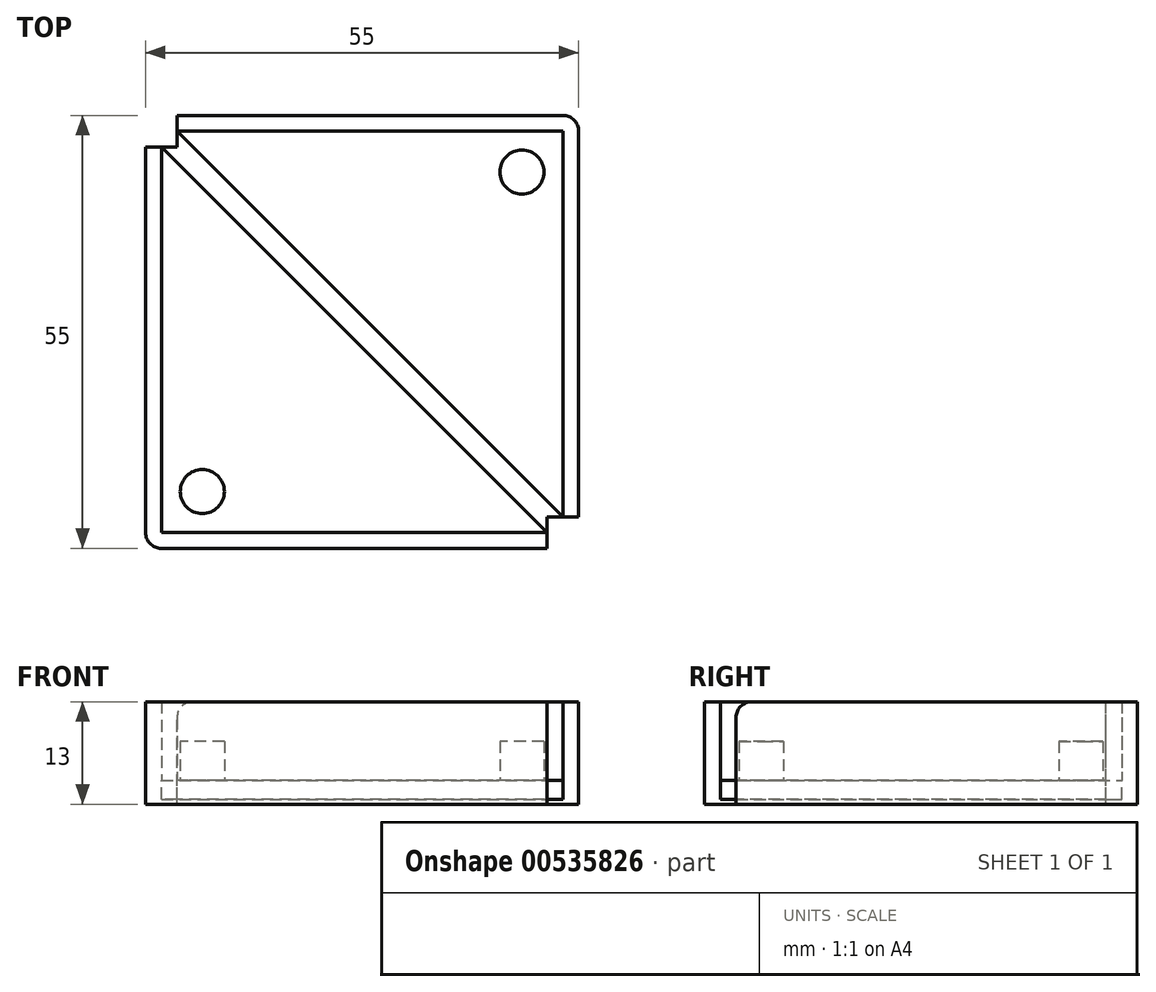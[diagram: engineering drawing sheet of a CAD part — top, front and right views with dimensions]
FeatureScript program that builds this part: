
annotation { "Feature Type Name" : "Feature", "Feature Type Description" : "" }
export const myFeature = defineFeature(function(context is Context, id is Id, definition is map)
    precondition{}
    {
        {
            var Q0;
            Q0=qCreatedBy(makeId("Top.planeOp"),FACE);
            var sketch = newSketch(context, id + "F0", { "sketchPlane" : qUnion([Q0])});
            skLineSegment(sketch, "E0.bottom", {"start": v(27.5, -27.5) * mm, "end": v(-27.5, -27.5) * mm});
            skLineSegment(sketch, "E0.top", {"start": v(27.5, 27.5) * mm, "end": v(-27.5, 27.5) * mm});
            skLineSegment(sketch, "E0.left", {"start": v(27.5, -27.5) * mm, "end": v(27.5, 27.5) * mm});
            skLineSegment(sketch, "E0.right", {"start": v(-27.5, -27.5) * mm, "end": v(-27.5, 27.5) * mm});
            skPoint(sketch, "E0.middle", {"position": v(0, 0) * mm});
            skSolve(sketch);
        }
        {
            var Q0;
            Q0=qSketchRegion(id+"F0",true);
            extrude(context, id + "F1", {"entities" : qUnion([Q0]), "depth" : 3 * mm, "offsetDistance" : 25 * mm});
        }
        {
            var Q0;
            Q0=makeQuery(id+"F1.opExtrude","CAP_FACE",FACE,{"disambiguationData":[OSD([sQuery(id+"F0.wireOp",EDGE,"E0.bottom"),sQuery(id+"F0.wireOp",EDGE,"E0.top"),sQuery(id+"F0.wireOp",EDGE,"E0.left"),sQuery(id+"F0.wireOp",EDGE,"E0.right")])],"isStart":false});
            var sketch = newSketch(context, id + "F2", { "sketchPlane" : qUnion([Q0])});
            skLineSegment(sketch, "E1.bottom", {"start": v(27.5, -27.5) * mm, "end": v(-27.5, -27.5) * mm});
            skLineSegment(sketch, "E1.top", {"start": v(27.5, 27.5) * mm, "end": v(-27.5, 27.5) * mm});
            skLineSegment(sketch, "E1.left", {"start": v(27.5, -27.5) * mm, "end": v(27.5, 27.5) * mm});
            skLineSegment(sketch, "E1.right", {"start": v(-27.5, -27.5) * mm, "end": v(-27.5, 27.5) * mm});
            skPoint(sketch, "E1.middle", {"position": v(0, 0) * mm});
            skLineSegment(sketch, "E2.bottom", {"start": v(25.5, -25.5) * mm, "end": v(-25.5, -25.5) * mm});
            skLineSegment(sketch, "E2.top", {"start": v(25.5, 25.5) * mm, "end": v(-25.5, 25.5) * mm});
            skLineSegment(sketch, "E2.left", {"start": v(25.5, -25.5) * mm, "end": v(25.5, 25.5) * mm});
            skLineSegment(sketch, "E2.right", {"start": v(-25.5, -25.5) * mm, "end": v(-25.5, 25.5) * mm});
            skSolve(sketch);
        }
        {
            var Q0;
            Q0=qSketchRegion(id+"F2",true);
            extrude(context, id + "F3", {"entities" : qUnion([Q0]), "operationType" : NewBodyOperationType.ADD, "depth" : 10 * mm, "offsetDistance" : 25 * mm});
        }
        {
            var Q0;
            Q0=makeQuery(id+"F1.opExtrude","CAP_FACE",FACE,{"disambiguationData":[OSD([sQuery(id+"F0.wireOp",EDGE,"E0.bottom"),sQuery(id+"F0.wireOp",EDGE,"E0.top"),sQuery(id+"F0.wireOp",EDGE,"E0.left"),sQuery(id+"F0.wireOp",EDGE,"E0.right")])],"isStart":false});
            var sketch = newSketch(context, id + "F4", { "sketchPlane" : qUnion([Q0])});
            skCircle(sketch, "E3", {"center": v(-20.3, -20.3) * mm, "radius": 2.8 * mm});
            skCircle(sketch, "E4", {"center": v(20.3, 20.3) * mm, "radius": 2.8 * mm});
            skSolve(sketch);
        }
        {
            var Q0;
            Q0=qSketchRegion(id+"F4",true);
            extrude(context, id + "F5", {"entities" : qUnion([Q0]), "operationType" : NewBodyOperationType.ADD, "depth" : 5 * mm, "offsetDistance" : 25 * mm});
        }
        {
            var Q0;
            Q0=makeQuery(id+"F3.opExtrude","CAP_FACE",FACE,{"disambiguationData":[OSD([sQuery(id+"F2.wireOp",EDGE,"E1.bottom"),sQuery(id+"F2.wireOp",EDGE,"E1.top"),sQuery(id+"F2.wireOp",EDGE,"E1.left"),sQuery(id+"F2.wireOp",EDGE,"E1.right"),sQuery(id+"F2.wireOp",EDGE,"E2.bottom"),sQuery(id+"F2.wireOp",EDGE,"E2.top"),sQuery(id+"F2.wireOp",EDGE,"E2.left"),sQuery(id+"F2.wireOp",EDGE,"E2.right")])],"isStart":false});
            var sketch = newSketch(context, id + "F6", { "sketchPlane" : qUnion([Q0])});
            skLineSegment(sketch, "E5.bottom", {"start": v(-27.5, 27.5) * mm, "end": v(-23.5, 27.5) * mm});
            skLineSegment(sketch, "E5.top", {"start": v(-27.5, 23.5) * mm, "end": v(-23.5, 23.5) * mm});
            skLineSegment(sketch, "E5.left", {"start": v(-27.5, 27.5) * mm, "end": v(-27.5, 23.5) * mm});
            skLineSegment(sketch, "E5.right", {"start": v(-23.5, 27.5) * mm, "end": v(-23.5, 23.5) * mm});
            skLineSegment(sketch, "E6.bottom", {"start": v(27.5, -27.5) * mm, "end": v(23.5, -27.5) * mm});
            skLineSegment(sketch, "E6.top", {"start": v(27.5, -23.5) * mm, "end": v(23.5, -23.5) * mm});
            skLineSegment(sketch, "E6.left", {"start": v(27.5, -27.5) * mm, "end": v(27.5, -23.5) * mm});
            skLineSegment(sketch, "E6.right", {"start": v(23.5, -27.5) * mm, "end": v(23.5, -23.5) * mm});
            skSolve(sketch);
        }
        {
            var Q0;
            Q0=qSketchRegion(id+"F6",true);
            extrude(context, id + "F7", {"entities" : qUnion([Q0]), "operationType" : NewBodyOperationType.REMOVE, "oppositeDirection" : true, "depth" : 25 * mm, "offsetDistance" : 25 * mm});
        }
        {
            var Q0;
            Q0=makeQuery(id+"F1.opExtrude","CAP_FACE",FACE,{"disambiguationData":[OSD([sQuery(id+"F0.wireOp",EDGE,"E0.bottom"),sQuery(id+"F0.wireOp",EDGE,"E0.top"),sQuery(id+"F0.wireOp",EDGE,"E0.left"),sQuery(id+"F0.wireOp",EDGE,"E0.right")])],"isStart":false});
            var sketch = newSketch(context, id + "F8", { "sketchPlane" : qUnion([Q0])});
            skLineSegment(sketch, "E7", {"start": v(-25.5, 23.5) * mm, "end": v(23.5, -25.5) * mm});
            skLineSegment(sketch, "E8", {"start": v(23.5, -25.5) * mm, "end": v(25.5, -23.5) * mm});
            skLineSegment(sketch, "E9", {"start": v(25.5, -23.5) * mm, "end": v(-23.5, 25.5) * mm});
            skLineSegment(sketch, "E10", {"start": v(-23.5, 25.5) * mm, "end": v(-25.5, 23.5) * mm});
            skSolve(sketch);
        }
        {
            var Q0;
            Q0=qSketchRegion(id+"F8",true);
            extrude(context, id + "F9", {"entities" : qUnion([Q0]), "operationType" : NewBodyOperationType.REMOVE, "oppositeDirection" : true, "depth" : 2.4 * mm, "offsetDistance" : 25 * mm});
        }
        {
            var Q0;
            Q0=makeQuery(id+"F7.boolean.opBoolean","COPY",EDGE,{"derivedFrom":makeQuery(id+"F7.opExtrude","CAP_EDGE",EDGE,{"disambiguationData":[OSD([sQuery(id+"F6.wireOp",EDGE,"E5.top")])],"isStart":true})});
            var Q1;
            Q1=makeQuery(id+"F7.boolean.opBoolean","COPY",EDGE,{"derivedFrom":makeQuery(id+"F7.opExtrude","CAP_EDGE",EDGE,{"disambiguationData":[OSD([sQuery(id+"F6.wireOp",EDGE,"E6.right")])],"isStart":true})});
            var Q2;
            Q2=makeQuery(id+"F7.boolean.opBoolean","COPY",EDGE,{"derivedFrom":makeQuery(id+"F7.opExtrude","CAP_EDGE",EDGE,{"disambiguationData":[OSD([sQuery(id+"F6.wireOp",EDGE,"E6.top")])],"isStart":true})});
            var Q3;
            Q3=makeQuery(id+"F7.boolean.opBoolean","COPY",EDGE,{"derivedFrom":makeQuery(id+"F7.opExtrude","CAP_EDGE",EDGE,{"disambiguationData":[OSD([sQuery(id+"F6.wireOp",EDGE,"E5.right")])],"isStart":true})});
            var Q4;
            Q4=makeQuery(id+"F7.boolean.opBoolean","COPY",EDGE,{"derivedFrom":makeQuery(id+"F7.opExtrude","SWEPT_EDGE",EDGE,{"disambiguationData":[OSD([sQuery(id+"F2.wireOp",EDGE,"E1.right"),sQuery(id+"F6.wireOp",EDGE,"E5.top"),sQuery(id+"F6.wireOp",EDGE,"E5.left")])]})});
            var Q5;
            Q5=makeQuery(id+"F7.boolean.opBoolean","COPY",EDGE,{"derivedFrom":makeQuery(id+"F7.opExtrude","SWEPT_EDGE",EDGE,{"disambiguationData":[OSD([sQuery(id+"F2.wireOp",EDGE,"E1.top"),sQuery(id+"F6.wireOp",EDGE,"E5.bottom"),sQuery(id+"F6.wireOp",EDGE,"E5.right")])]})});
            var Q6;
            Q6=makeQuery(id+"F7.boolean.opBoolean","COPY",EDGE,{"derivedFrom":makeQuery(id+"F7.opExtrude","SWEPT_EDGE",EDGE,{"disambiguationData":[OSD([sQuery(id+"F2.wireOp",EDGE,"E1.bottom"),sQuery(id+"F6.wireOp",EDGE,"E6.bottom"),sQuery(id+"F6.wireOp",EDGE,"E6.right")])]})});
            var Q7;
            Q7=makeQuery(id+"F7.boolean.opBoolean","COPY",EDGE,{"derivedFrom":makeQuery(id+"F7.opExtrude","SWEPT_EDGE",EDGE,{"disambiguationData":[OSD([sQuery(id+"F2.wireOp",EDGE,"E1.left"),sQuery(id+"F6.wireOp",EDGE,"E6.top"),sQuery(id+"F6.wireOp",EDGE,"E6.left")])]})});
            var Q8;
            Q8=makeQuery(id+"F3.boolean.opBoolean","MERGE",EDGE,{"derivedFrom":[makeQuery(id+"F1.opExtrude","SWEPT_EDGE",EDGE,{"disambiguationData":[OSD([sQuery(id+"F0.wireOp",EDGE,"E0.bottom"),sQuery(id+"F0.wireOp",EDGE,"E0.right")])]}),makeQuery(id+"F3.opExtrude","SWEPT_EDGE",EDGE,{"disambiguationData":[OSD([sQuery(id+"F2.wireOp",EDGE,"E1.bottom"),sQuery(id+"F2.wireOp",EDGE,"E1.right")])]})]});
            var Q9;
            Q9=makeQuery(id+"F3.boolean.opBoolean","MERGE",EDGE,{"derivedFrom":[makeQuery(id+"F1.opExtrude","SWEPT_EDGE",EDGE,{"disambiguationData":[OSD([sQuery(id+"F0.wireOp",EDGE,"E0.top"),sQuery(id+"F0.wireOp",EDGE,"E0.left")])]}),makeQuery(id+"F3.opExtrude","SWEPT_EDGE",EDGE,{"disambiguationData":[OSD([sQuery(id+"F2.wireOp",EDGE,"E1.top"),sQuery(id+"F2.wireOp",EDGE,"E1.left")])]})]});
            fillet(context, id + "F10", {"entities" : qUnion([Q0, Q1, Q2, Q3, Q4, Q5, Q6, Q7, Q8, Q9]), "radius" : 2 * mm, "tangentPropagation" : true, "allowEdgeOverflow" : false});
        }
    });
